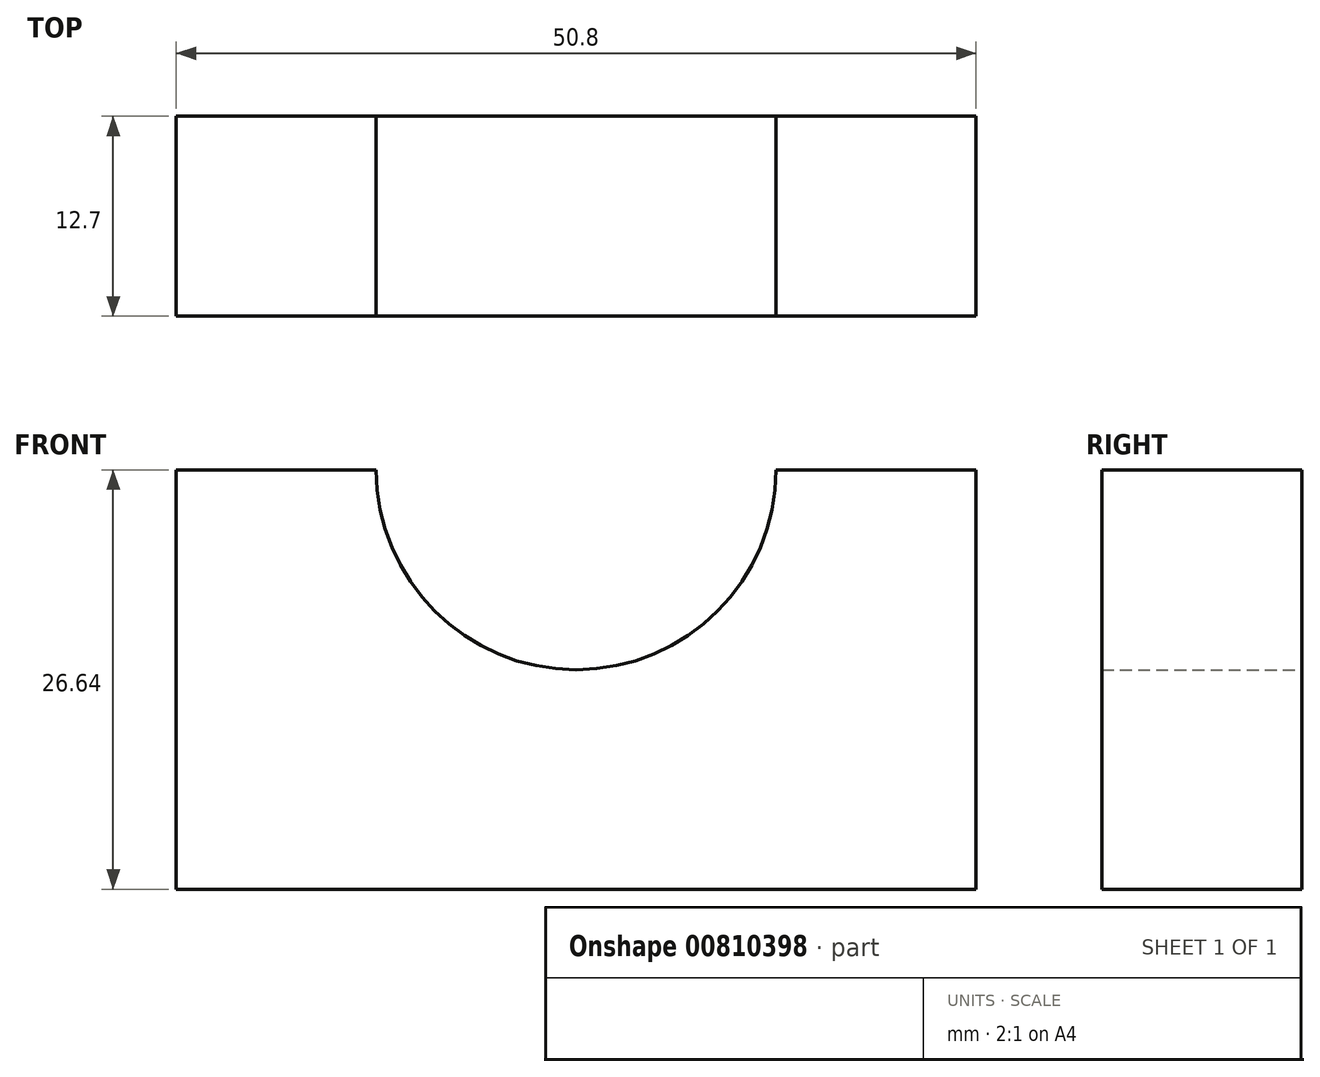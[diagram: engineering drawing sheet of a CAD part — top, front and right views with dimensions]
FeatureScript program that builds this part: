
annotation { "Feature Type Name" : "Feature", "Feature Type Description" : "" }
export const myFeature = defineFeature(function(context is Context, id is Id, definition is map)
    precondition{}
    {
        {
            var Q0;
            Q0=qCreatedBy(makeId("Front.planeOp"),FACE);
            var sketch = newSketch(context, id + "F0", { "sketchPlane" : qUnion([Q0])});
            skArc(sketch, "E0", {"start": v(-12.7, 26.64) * mm, "mid": v(0, 13.94) * mm, "end": v(12.7, 26.64) * mm});
            skLineSegment(sketch, "E1.bottom", {"start": v(-25.4, 26.64) * mm, "end": v(-12.7, 26.64) * mm});
            skLineSegment(sketch, "E1.top", {"start": v(-25.4, 0) * mm, "end": v(25.4, 0) * mm});
            skLineSegment(sketch, "E1.left", {"start": v(-25.4, 26.64) * mm, "end": v(-25.4, 0) * mm});
            skLineSegment(sketch, "E1.right", {"start": v(25.4, 26.64) * mm, "end": v(25.4, 0) * mm});
            skPoint(sketch, "E2", {"position": v(-12.7, 26.64) * mm});
            skPoint(sketch, "E3", {"position": v(12.7, 26.64) * mm});
            skLineSegment(sketch, "E4.trimOffspring", {"start": v(12.7, 26.64) * mm, "end": v(25.4, 26.64) * mm});
            skSolve(sketch);
        }
        {
            var Q0;
            Q0=makeQuery(id+"F0.imprint","IMPRINT",FACE,{"disambiguationData":[TD([[makeQuery(id+"F0.imprint","IMPRINT",EDGE,{"derivedFrom":sQuery(id+"F0.wireOp",EDGE,"E0")}),-1.0]])]});
            extrude(context, id + "F1", {"entities" : qUnion([Q0]), "depth" : 12.7 * mm, "offsetDistance" : 25.4 * mm});
        }
    });
